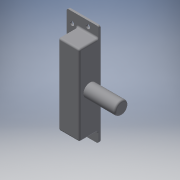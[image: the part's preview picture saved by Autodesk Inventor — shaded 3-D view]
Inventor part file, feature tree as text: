
AUTODESK INVENTOR PART (.ipt)
format: ipt  version: 2018 (Build 220112000, 112)  size: 210,432 bytes
history: native  units: in
note: dims shown in document units (in); Inventor stores cm internally (conversion verified against a paired STEP export)
features: extrude x4, sketch x4, fillet x3, other x3, reference x2
ambient origin geometry x8: Origin, YZ Plane, XZ Plane, XY Plane, X Axis, Y Axis, Z Axis, Center Point
bodies: Solid1 (feature_tree)
feature tree (16):
  extrude  "Extrusion1"  Depth=0.5in
  extrude  "Extrusion2"  Depth=0.25in
  extrude  "Extrusion3"  Depth=0.25in
  extrude  "Extrusion4"  Depth=0.0394in
  fillet  "Fillet1"  Radius=0.1181in
  fillet  "Fillet2"  Radius=0.5in
  fillet  "Fillet3"  Radius=1.199in
  sketch  "Sketch1"  dims[d0=0.75in d1=0.5in]
  reference  "Reference1"
  reference  "Reference2"
  sketch  "Sketch2"  dims[d2=0.125in d3=0.25in]
  sketch  "Sketch3"  dims[d4=0.1181in d5=0.25in]
  sketch  "Sketch4"  dims[d6=0.1181in d7=0.949in d8=0.1181in d9=0.5in d10=0.0in d11=1.199in d12=0.25in d13=0.311in d14=0.75in d15=0.0in d16=0.75in d17=0.5in d18=0.125in d19=0.25in d20=0.1181in d21=0.25in d22=0.1181in d23=0.949in d24=0.1181in d25=0.45in d26=0.0in d27=2.3985in d28=0.25in d29=0.25in d30=0.75in d31=0.5in d32=0.125in d33=0.25in d34=0.0984in d35=0.25in d36=0.0984in d37=0.949in d38=0.0984in d39=0.25in d40=0.25in d41=0.0984in d42=0.0984in d43=0.45in d44=0.0in d45=0.0394in d46=0.0394in d47=0.0394in]
  other  "<userpath>\OneDrive\Documents\Inventor\TSA\2018\Animatronics\Tortoise\AssemblyTURTLE.iam"
  other  "AssemblyTURTLE.iam"
  other  "Frame:1"
